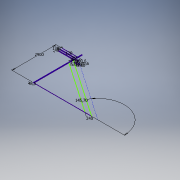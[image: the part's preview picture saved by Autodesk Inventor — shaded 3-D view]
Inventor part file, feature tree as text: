
AUTODESK INVENTOR PART (.ipt)
format: ipt  version: 2018 (Build 220112000, 112)  size: 108,544 bytes
history: native  units: mm
features: sketch x1
ambient origin geometry x8: Origin, YZ Plane, XZ Plane, XY Plane, X Axis, Y Axis, Z Axis, Center Point
feature tree (1):
  sketch  "Sketch1"  dims[d1=48.5mm d3=120.0mm d4=40.0mm d5=40.0mm d6=130.0mm d7=35.0mm d8=35.0mm d9=2900.0mm d11=250.0mm d12=170.6mm d13=5.986479mm d14=80.0mm d15=250.0mm d16=80.0mm d17=170.6mm d18=240.0mm]
